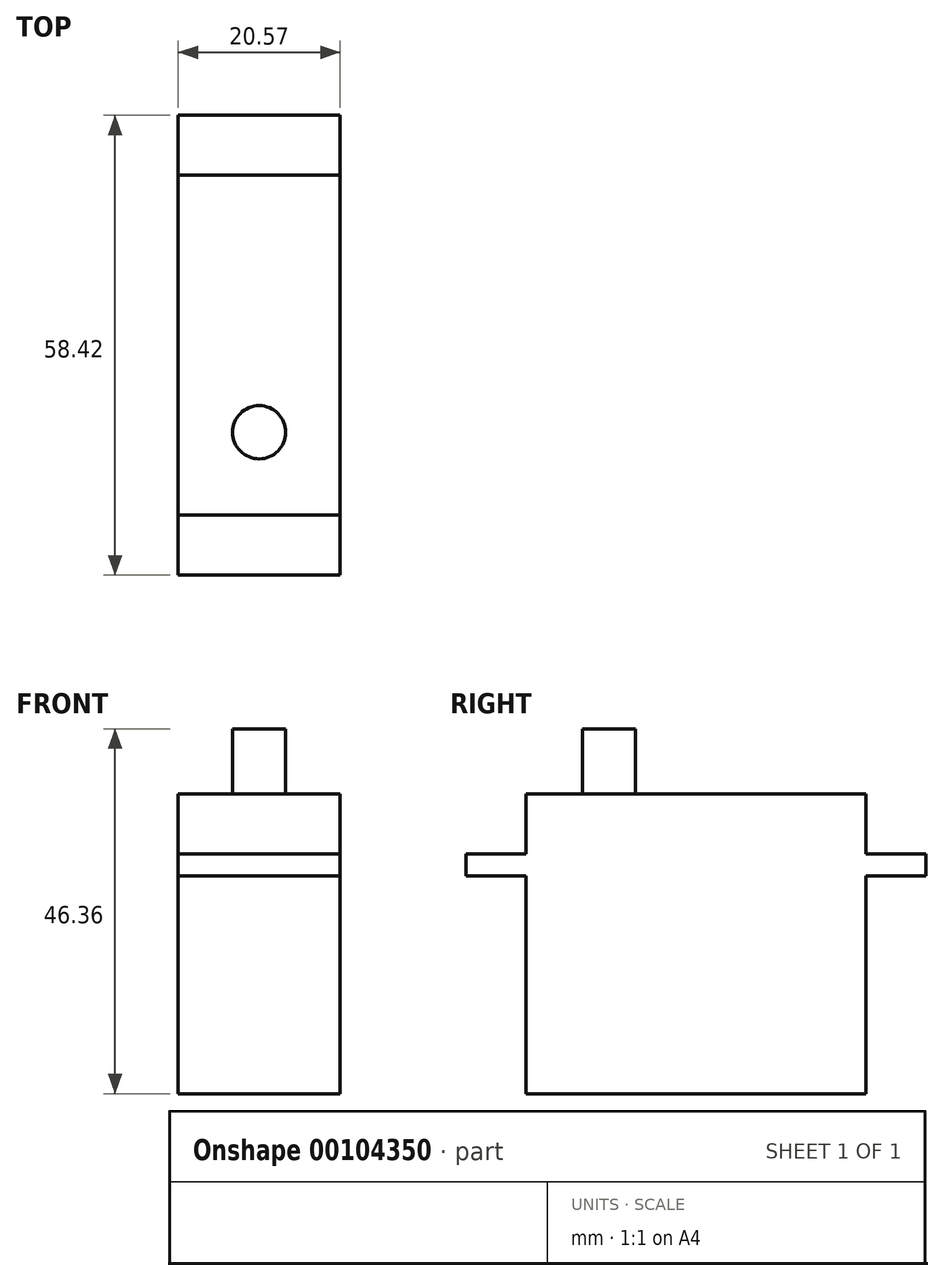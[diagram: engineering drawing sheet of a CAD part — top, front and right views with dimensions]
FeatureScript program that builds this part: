
annotation { "Feature Type Name" : "Feature", "Feature Type Description" : "" }
export const myFeature = defineFeature(function(context is Context, id is Id, definition is map)
    precondition{}
    {
        {
            var Q0;
            Q0=qCreatedBy(makeId("Right.planeOp"),FACE);
            var sketch = newSketch(context, id + "F0", { "sketchPlane" : qUnion([Q0])});
            skLineSegment(sketch, "E0", {"start": v(0, 0) * mm, "end": v(43.18, 0) * mm});
            skLineSegment(sketch, "E1", {"start": v(43.18, 0) * mm, "end": v(43.18, 27.69) * mm});
            skLineSegment(sketch, "E2", {"start": v(43.18, 27.69) * mm, "end": v(50.8, 27.69) * mm});
            skLineSegment(sketch, "E3", {"start": v(50.8, 27.69) * mm, "end": v(50.8, 30.48) * mm});
            skLineSegment(sketch, "E4", {"start": v(50.8, 30.48) * mm, "end": v(43.18, 30.48) * mm});
            skLineSegment(sketch, "E5", {"start": v(43.18, 30.48) * mm, "end": v(43.18, 38.1) * mm});
            skLineSegment(sketch, "E6", {"start": v(43.18, 38.1) * mm, "end": v(0, 38.1) * mm});
            skLineSegment(sketch, "E7", {"start": v(0, 38.1) * mm, "end": v(0, 30.48) * mm});
            skLineSegment(sketch, "E8", {"start": v(0, 30.48) * mm, "end": v(-7.62, 30.48) * mm});
            skLineSegment(sketch, "E9", {"start": v(-7.62, 30.48) * mm, "end": v(-7.62, 27.69) * mm});
            skLineSegment(sketch, "E10", {"start": v(-7.62, 27.69) * mm, "end": v(0, 27.69) * mm});
            skLineSegment(sketch, "E11", {"start": v(0, 27.69) * mm, "end": v(0, 0) * mm});
            skSolve(sketch);
        }
        {
            var Q0;
            Q0 = qSketchRegion(id + "F0", true);
            extrude(context, id + "F1", {"entities" : qUnion([Q0]), "depth" : 20.57 * mm});
        }
        {
            var Q0;
            Q0=makeQuery(id+"F1.opExtrude","SWEPT_FACE",FACE,{"disambiguationData":[OSD([sQuery(id+"F0.wireOp",EDGE,"E6")])]});
            var sketch = newSketch(context, id + "F2", { "sketchPlane" : qUnion([Q0])});
            skCircle(sketch, "E12", {"center": v(10.29, 10.54) * mm, "radius": 3.38 * mm});
            skPoint(sketch, "E13", {"position": v(10.29, 0) * mm});
            skSolve(sketch);
        }
        {
            var Q0;
            Q0 = qSketchRegion(id + "F2", true);
            extrude(context, id + "F3", {"entities" : qUnion([Q0]), "operationType" : NewBodyOperationType.ADD, "depth" : 8.25 * mm});
        }
    });
